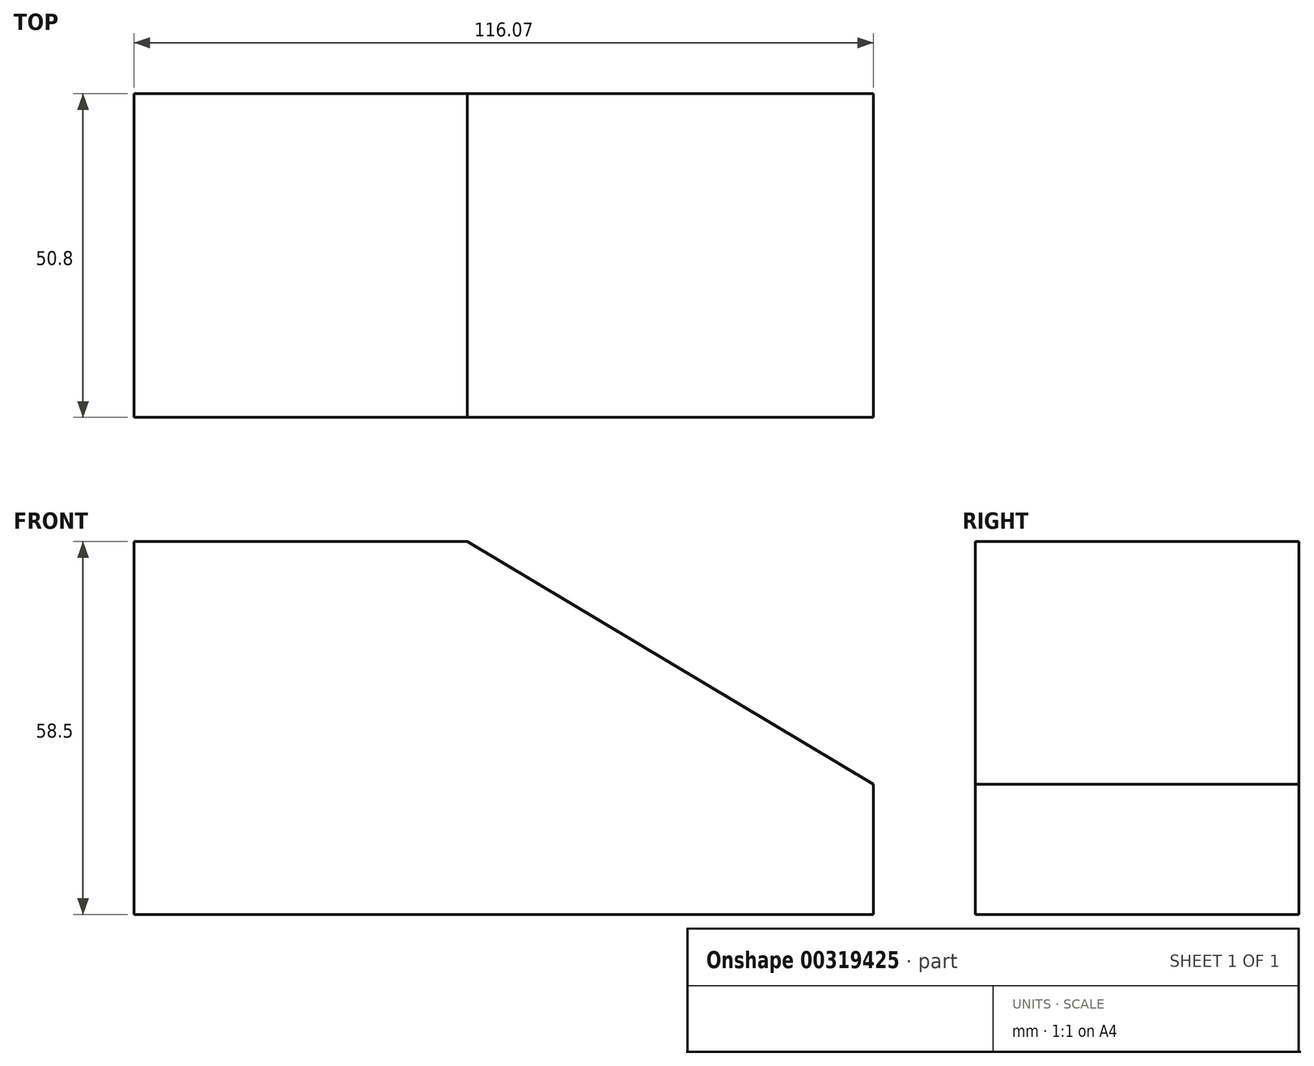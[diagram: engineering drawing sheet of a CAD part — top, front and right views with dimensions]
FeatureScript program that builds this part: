
annotation { "Feature Type Name" : "Feature", "Feature Type Description" : "" }
export const myFeature = defineFeature(function(context is Context, id is Id, definition is map)
    precondition{}
    {
        {
            var Q0;
            Q0=qCreatedBy(makeId("Front.planeOp"),FACE);
            var sketch = newSketch(context, id + "F0", { "sketchPlane" : qUnion([Q0])});
            skLineSegment(sketch, "E0", {"start": v(52.3, -44.73) * mm, "end": v(52.3, -24.3) * mm});
            skLineSegment(sketch, "E1", {"start": v(52.3, -24.3) * mm, "end": v(-11.45, 13.77) * mm});
            skLineSegment(sketch, "E2", {"start": v(-11.45, 13.77) * mm, "end": v(-63.76, 13.77) * mm});
            skLineSegment(sketch, "E3", {"start": v(-63.76, 13.77) * mm, "end": v(-63.76, -44.73) * mm});
            skLineSegment(sketch, "E4", {"start": v(-63.76, -44.73) * mm, "end": v(52.3, -44.73) * mm});
            skSolve(sketch);
        }
        {
            var Q0;
            Q0=makeQuery(id+"F0.imprint","IMPRINT",FACE,{"disambiguationData":[TD([[makeQuery(id+"F0.imprint","IMPRINT",EDGE,{"derivedFrom":sQuery(id+"F0.wireOp",EDGE,"E0")}),1.0]])]});
            extrude(context, id + "F1", {"entities" : qUnion([Q0]), "depth" : 50.8 * mm});
        }
    });
